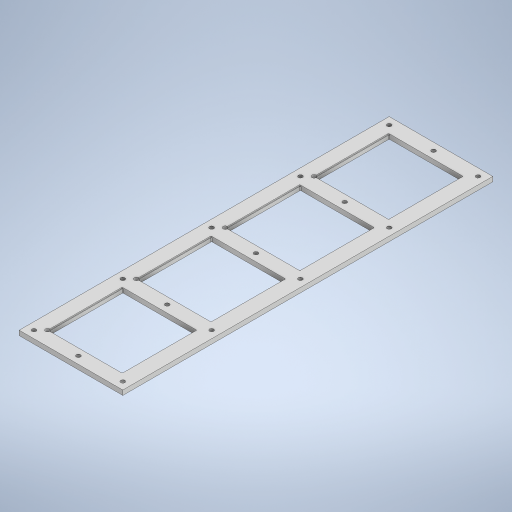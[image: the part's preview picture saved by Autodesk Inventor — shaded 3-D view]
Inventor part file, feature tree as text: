
AUTODESK INVENTOR PART (.ipt)
format: ipt  version: 2023 (Build 270158000, 158)  size: 440,320 bytes
history: native  units: in
note: dims shown in document units (in); Inventor stores cm internally (conversion verified against a paired STEP export)
features: sketch x5, extrude x4, hole x1, projected_geometry x1
ambient origin geometry x8: Origin, YZ Plane, XZ Plane, XY Plane, X Axis, Y Axis, Z Axis, Center Point
bodies: Solid1 (feature_tree)
feature tree (11):
  extrude  "Extrusion1"  Depth=4.9213in
  extrude  "Extrusion2"  Depth=0.1969in
  extrude  "Extrusion3"  Depth=0.9843in
  extrude  "Extrusion4"  TaperAngle=0.0deg  [1 undecoded]
  hole  "Hole1"  [1 undecoded]
  sketch  "Sketch1"  dims[d0=1.378in d1=4.9213in]
  sketch  "Sketch2"  dims[d2=0.0625in d3=0.0in d4=0.1969in]
  sketch  "Sketch3"  dims[d5=0.1969in d6=0.9843in]
  sketch  "Sketch4"  dims[d7=0.9843in d8=0.0in d9=0.0in]
  projected_geometry  "Projected Loop1"
  sketch  "Sketch5"  dims[d11=0.9921in d13=0.0138in d14=0.0in d16=0.0in d17=0.0in d18=0.0098in d19=1.5748in d21=1.1811in d22=0.3937in d24=0.3937in d26=0.0098in d27=1.5748in d29=1.1811in d30=0.3937in d32=0.3937in d34=0.0591in d35=1.5748in d37=1.1811in d38=0.3937in d40=0.3937in d42=0.0079in d43=0.0984in d44=0.0984in d45=0.0984in d46=1.9685in d48=1.1811in d49=0.3937in d51=0.3937in d53=0.0561in d54=0.146in d55=0.1575in d56=0.0787in d57=90.0deg d58=0.315in d59=0.8108in d15=0.0197in d20=0.0in]
note: 2 required parameter values undecoded (feature->parameter linkage not recoverable at this tier; creation-order binding heuristic only, values carry confidence <= 0.55)
